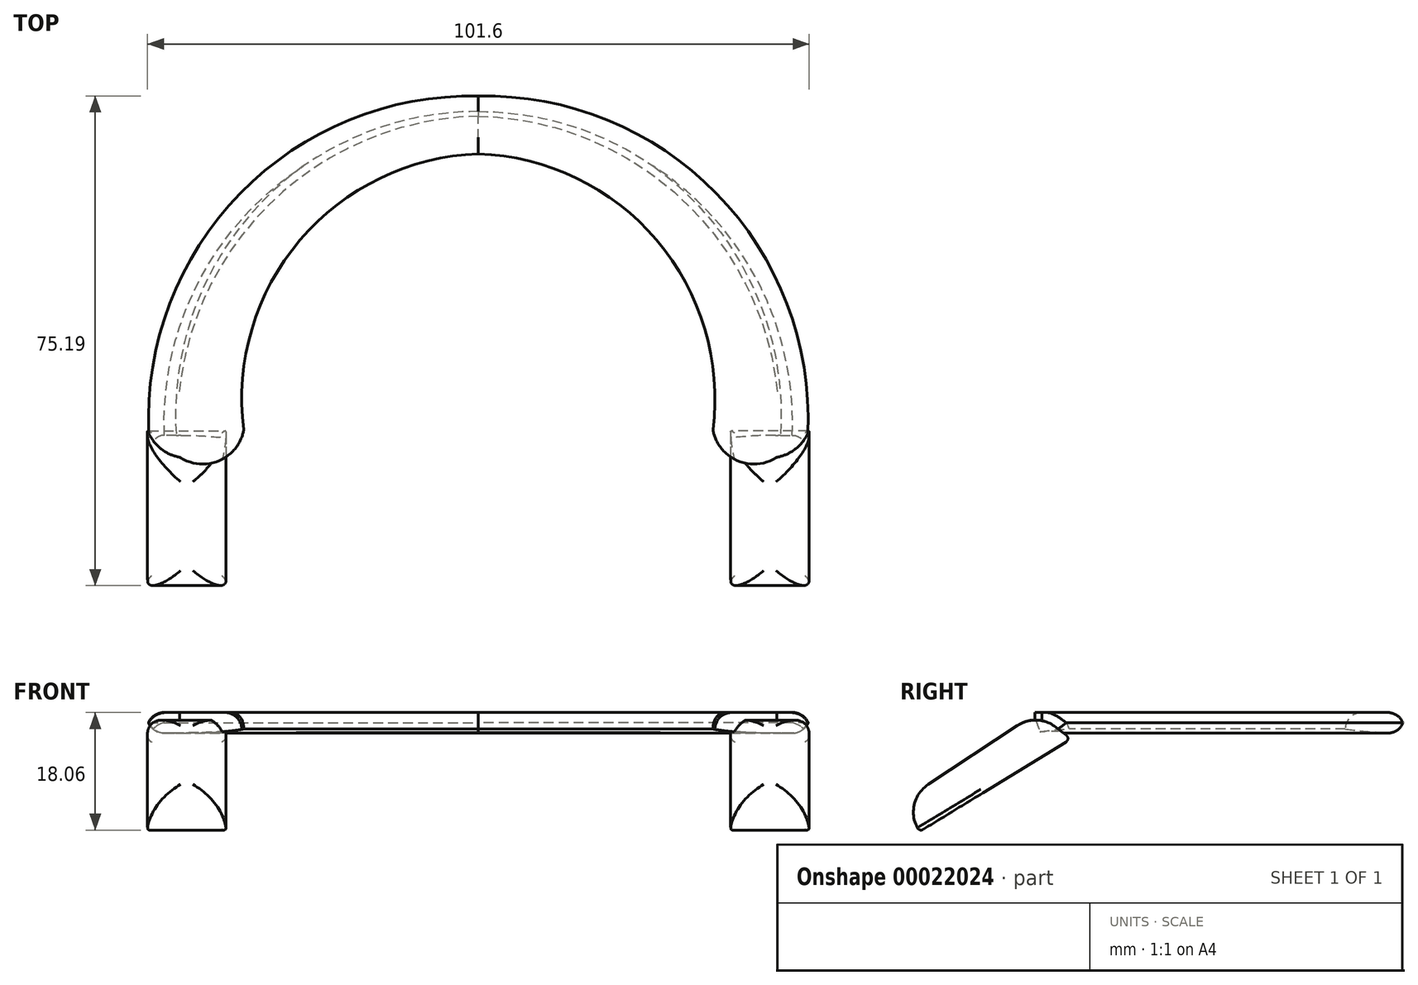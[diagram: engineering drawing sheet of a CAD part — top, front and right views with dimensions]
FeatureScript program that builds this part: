
annotation { "Feature Type Name" : "Feature", "Feature Type Description" : "" }
export const myFeature = defineFeature(function(context is Context, id is Id, definition is map)
    precondition{}
    {
        {
            var Q0;
            Q0=qCreatedBy(makeId("Top.planeOp"),FACE);
            var sketch = newSketch(context, id + "F0", { "sketchPlane" : qUnion([Q0])});
            skArc(sketch, "E0", {"start": v(0, 0) * mm, "mid": v(-49.71, 51.45) * mm, "end": v(-99.42, 0) * mm});
            skArc(sketch, "E1", {"start": v(-99.42, 0) * mm, "mid": v(-93.12, -5.27) * mm, "end": v(-86.82, 0) * mm});
            skArc(sketch, "E2", {"start": v(-12.15, 0) * mm, "mid": v(-6.07, -4.3) * mm, "end": v(0, 0) * mm});
            skArc(sketch, "E3", {"start": v(-12.15, 0) * mm, "mid": v(-49.49, 42.41) * mm, "end": v(-86.82, 0) * mm});
            skSolve(sketch);
        }
        {
            var Q0;
            Q0=makeQuery(id+"F0.imprint","IMPRINT",FACE,{"disambiguationData":[TD([[makeQuery(id+"F0.imprint","IMPRINT",EDGE,{"derivedFrom":sQuery(id+"F0.wireOp",EDGE,"E0")}),1.0]])]});
            extrude(context, id + "F1", {"entities" : qUnion([Q0]), "depth" : 3.17 * mm});
        }
        {
            var Q0;
            Q0=makeQuery(id+"F1.opExtrude","CAP_EDGE",EDGE,{"disambiguationData":[OSD([sQuery(id+"F0.wireOp",EDGE,"E0")])],"isStart":true});
            var Q1;
            Q1=makeQuery(id+"F1.opExtrude","CAP_EDGE",EDGE,{"disambiguationData":[OSD([sQuery(id+"F0.wireOp",EDGE,"E3")])],"isStart":false});
            var Q2;
            Q2=makeQuery(id+"F1.opExtrude","CAP_EDGE",EDGE,{"disambiguationData":[OSD([sQuery(id+"F0.wireOp",EDGE,"E0")])],"isStart":false});
            fillet(context, id + "F2", {"entities" : qUnion([Q0, Q1, Q2]), "radius" : 2.54 * mm, "tangentPropagation" : true, "allowEdgeOverflow" : false});
        }
        {
            var Q0;
            Q0=makeQuery(id+"F1.opExtrude","CAP_EDGE",EDGE,{"disambiguationData":[OSD([sQuery(id+"F0.wireOp",EDGE,"E3")])],"isStart":true});
            fillet(context, id + "F3", {"entities" : qUnion([Q0]), "radius" : 73.66 * mm, "tangentPropagation" : true, "allowEdgeOverflow" : false});
        }
        {
            var Q0;
            Q0=qCreatedBy(makeId("Right.planeOp"),FACE);
            var sketch = newSketch(context, id + "F4", { "sketchPlane" : qUnion([Q0])});
            skLineSegment(sketch, "E4", {"start": v(-4.94, 3.18) * mm, "end": v(-26.43, -11.05) * mm});
            skLineSegment(sketch, "E5", {"start": v(0.3, -0.88) * mm, "end": v(-22.94, -15.11) * mm});
            skLineSegment(sketch, "E6", {"start": v(-22.94, -15.11) * mm, "end": v(-26.43, -11.05) * mm});
            skLineSegment(sketch, "E7", {"start": v(0.3, -0.88) * mm, "end": v(-4.94, 3.18) * mm});
            skSolve(sketch);
        }
        {
            var Q0;
            Q0 = qSketchRegion(id + "F4", true);
            extrude(context, id + "F5", {"entities" : qUnion([Q0]), "operationType" : NewBodyOperationType.ADD, "oppositeDirection" : true, "depth" : 12.06 * mm});
        }
        {
            var Q0;
            Q0=makeQuery(id+"F5.opExtrude","SWEPT_FACE",FACE,{"disambiguationData":[OSD([sQuery(id+"F4.wireOp",EDGE,"E4")])]});
            fillet(context, id + "F6", {"entities" : qUnion([Q0]), "radius" : 5.08 * mm, "tangentPropagation" : true, "allowEdgeOverflow" : false});
        }
        {
            var Q0;
            Q0=makeQuery(id+"F5.opExtrude","SWEPT_FACE",FACE,{"disambiguationData":[OSD([sQuery(id+"F4.wireOp",EDGE,"E5")])]});
            fillet(context, id + "F7", {"entities" : qUnion([Q0]), "radius" : 0.64 * mm, "tangentPropagation" : true, "allowEdgeOverflow" : false});
        }
        {
            var Q0;
            Q0=qCreatedBy(makeId("Right.planeOp"),FACE);
            cPlane(context, id + "F8", {"entities" : qUnion([Q0]), "cplaneType" : CPlaneType.OFFSET, "offset" : 50.8 * mm, "oppositeDirection" : true, "width" : 152.4 * mm, "height" : 152.4 * mm});
        }
        {
            var Q0;
            Q0=makeQuery(id+"F1.opExtrude","SWEPT_BODY",BODY,{"disambiguationData":[OSD([sQuery(id+"F0.wireOp",EDGE,"E0"),sQuery(id+"F0.wireOp",EDGE,"E1"),sQuery(id+"F0.wireOp",EDGE,"E2"),sQuery(id+"F0.wireOp",EDGE,"E3")])]});
            var Q1;
            Q1=qCreatedBy(id+"F8.planeOp",FACE);
            mirror(context, id + "F9", {"operationType" : NewBodyOperationType.ADD, "entities" : qUnion([Q0]), "mirrorPlane" : qUnion([Q1])});
        }
    });
